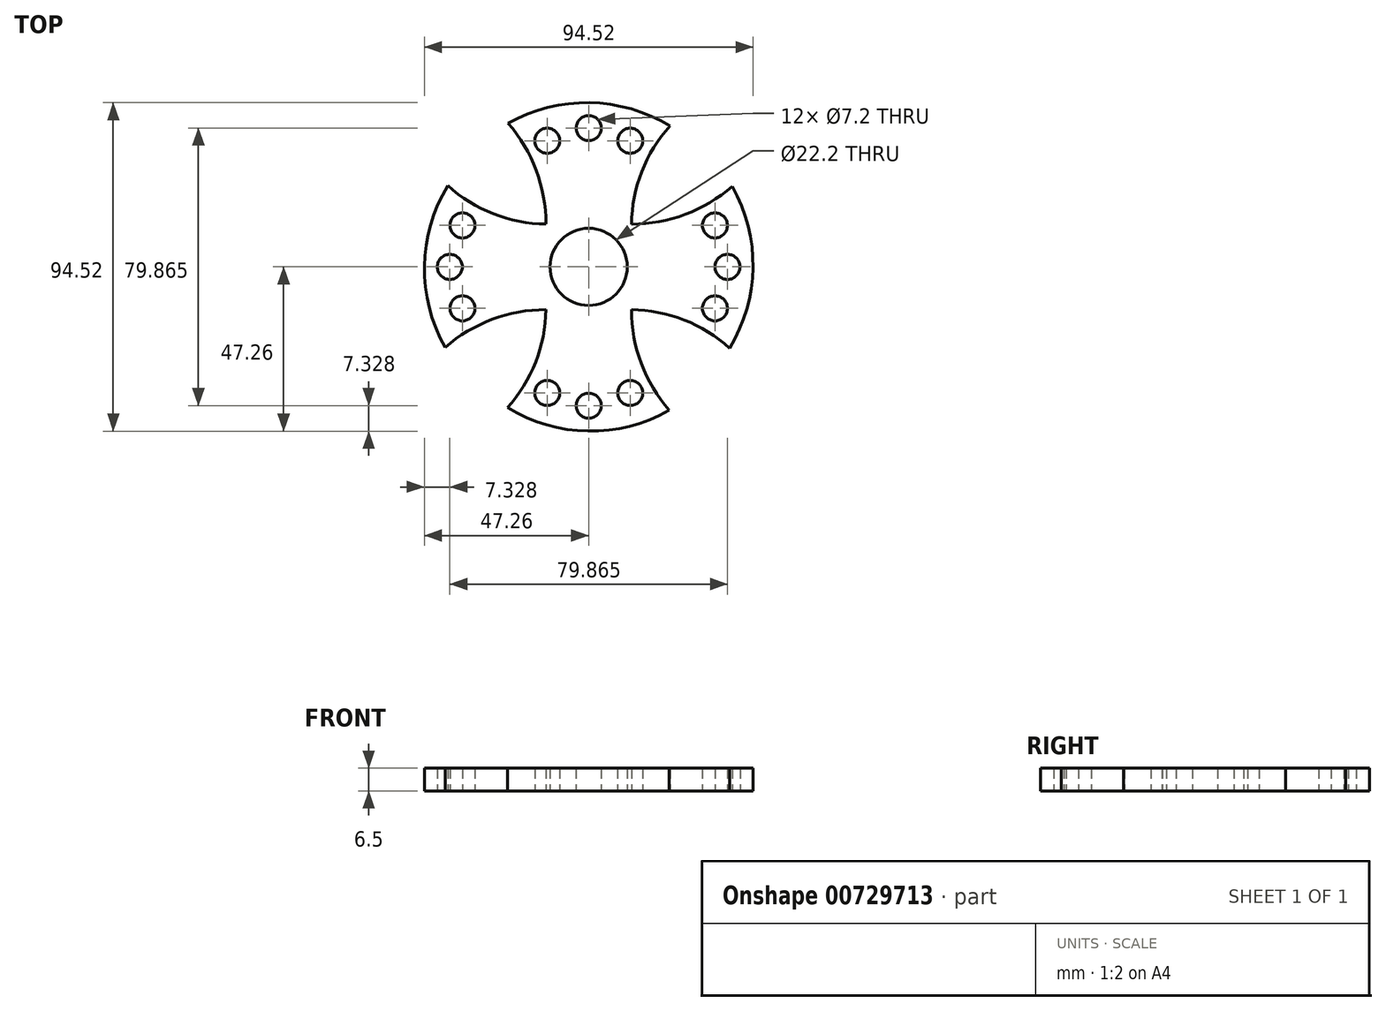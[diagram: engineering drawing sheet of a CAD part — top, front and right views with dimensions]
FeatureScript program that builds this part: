
annotation { "Feature Type Name" : "Feature", "Feature Type Description" : "" }
export const myFeature = defineFeature(function(context is Context, id is Id, definition is map)
    precondition{}
    {
        {
            var Q0;
            Q0=qCreatedBy(makeId("Top.planeOp"),FACE);
            var sketch = newSketch(context, id + "F0", { "sketchPlane" : qUnion([Q0])});
            skCircle(sketch, "E0", {"center": v(0, 0) * mm, "radius": 11.1 * mm});
            skCircle(sketch, "E1", {"center": v(0, 0) * mm, "radius": 14 * mm});
            skCircle(sketch, "E2", {"center": v(0, 39.93) * mm, "radius": 3.6 * mm});
            skCircle(sketch, "E3", {"center": v(-11.93, 36.3) * mm, "radius": 3.6 * mm});
            skArc(sketch, "E4", {"start": v(-14, 0) * mm, "mid": v(-13.33, 21.8) * mm, "end": v(-23.15, 41.28) * mm});
            skArc(sketch, "E5", {"start": v(23.39, 40.5) * mm, "mid": v(13.42, 21.48) * mm, "end": v(14, 0) * mm});
            skArc(sketch, "E6", {"start": v(23.39, 40.5) * mm, "mid": v(0.22, 47.25) * mm, "end": v(-23.15, 41.28) * mm});
            skCircle(sketch, "E7.MirrorC", {"center": v(11.93, 36.3) * mm, "radius": 3.6 * mm});
            skArc(sketch, "E8.1.0", {"start": v(-40.5, 23.39) * mm, "mid": v(-47.25, 0.22) * mm, "end": v(-41.28, -23.15) * mm});
            skCircle(sketch, "E8.1.1", {"center": v(-39.93, 0) * mm, "radius": 3.6 * mm});
            skCircle(sketch, "E8.1.2", {"center": v(-36.3, 11.93) * mm, "radius": 3.6 * mm});
            skCircle(sketch, "E8.1.3", {"center": v(-36.3, -11.93) * mm, "radius": 3.6 * mm});
            skArc(sketch, "E8.1.4", {"start": v(0, -14) * mm, "mid": v(-21.8, -13.33) * mm, "end": v(-41.28, -23.15) * mm});
            skArc(sketch, "E8.1.5", {"start": v(-40.5, 23.39) * mm, "mid": v(-21.48, 13.42) * mm, "end": v(0, 14) * mm});
            skArc(sketch, "E8.2.0", {"start": v(-23.39, -40.5) * mm, "mid": v(-0.22, -47.25) * mm, "end": v(23.15, -41.28) * mm});
            skCircle(sketch, "E8.2.1", {"center": v(0, -39.93) * mm, "radius": 3.6 * mm});
            skCircle(sketch, "E8.2.2", {"center": v(-11.93, -36.3) * mm, "radius": 3.6 * mm});
            skCircle(sketch, "E8.2.3", {"center": v(11.93, -36.3) * mm, "radius": 3.6 * mm});
            skArc(sketch, "E8.2.4", {"start": v(14, 0) * mm, "mid": v(13.33, -21.8) * mm, "end": v(23.15, -41.28) * mm});
            skArc(sketch, "E8.2.5", {"start": v(-23.39, -40.5) * mm, "mid": v(-13.42, -21.48) * mm, "end": v(-14, 0) * mm});
            skArc(sketch, "E8.3.0", {"start": v(40.5, -23.39) * mm, "mid": v(47.25, -0.22) * mm, "end": v(41.28, 23.15) * mm});
            skCircle(sketch, "E8.3.1", {"center": v(39.93, 0) * mm, "radius": 3.6 * mm});
            skCircle(sketch, "E8.3.2", {"center": v(36.3, -11.93) * mm, "radius": 3.6 * mm});
            skCircle(sketch, "E8.3.3", {"center": v(36.3, 11.93) * mm, "radius": 3.6 * mm});
            skArc(sketch, "E8.3.4", {"start": v(0, 14) * mm, "mid": v(21.8, 13.33) * mm, "end": v(41.28, 23.15) * mm});
            skArc(sketch, "E8.3.5", {"start": v(40.5, -23.39) * mm, "mid": v(21.48, -13.42) * mm, "end": v(0, -14) * mm});
            skSolve(sketch);
        }
        {
            var Q0;
            {var subQ0=sQuery(id+"F0.wireOp",EDGE,"E8.1.5");var subQ1=sQuery(id+"F0.wireOp",EDGE,"E1");var subQ3=makeQuery(id+"F0.imprint","INTERSECT",VERTEX,{"derivedFrom":[subQ1,subQ0]});Q0=makeQuery(id+"F0.imprint","IMPRINT",FACE,{"disambiguationData":[TD([[makeQuery(id+"F0.imprint","IMPRINT",EDGE,{"disambiguationData":[TD([[subQ3,1.0]])],"derivedFrom":subQ1}),1.0]])]});}
            var Q1;
            {var subQ0=sQuery(id+"F0.wireOp",EDGE,"E8.3.4");var subQ1=sQuery(id+"F0.wireOp",EDGE,"E1");var subQ3=makeQuery(id+"F0.imprint","INTERSECT",VERTEX,{"derivedFrom":[subQ1,subQ0]});Q1=makeQuery(id+"F0.imprint","IMPRINT",FACE,{"disambiguationData":[TD([[makeQuery(id+"F0.imprint","IMPRINT",EDGE,{"disambiguationData":[TD([[subQ3,-1.0]])],"derivedFrom":subQ1}),1.0]])]});}
            var Q2;
            {var subQ6=sQuery(id+"F0.wireOp",EDGE,"E8.3.0");Q2=makeQuery(id+"F0.imprint","IMPRINT",FACE,{"disambiguationData":[TD([[makeQuery(id+"F0.imprint","IMPRINT",EDGE,{"derivedFrom":subQ6}),1.0]])]});}
            var Q3;
            {var subQ0=sQuery(id+"F0.wireOp",EDGE,"E8.2.4");var subQ1=sQuery(id+"F0.wireOp",EDGE,"E1");var subQ3=makeQuery(id+"F0.imprint","INTERSECT",VERTEX,{"derivedFrom":[subQ1,subQ0]});Q3=makeQuery(id+"F0.imprint","IMPRINT",FACE,{"disambiguationData":[TD([[makeQuery(id+"F0.imprint","IMPRINT",EDGE,{"disambiguationData":[TD([[subQ3,-1.0]])],"derivedFrom":subQ1}),1.0]])]});}
            var Q4;
            {var subQ0=sQuery(id+"F0.wireOp",EDGE,"E5");var subQ1=sQuery(id+"F0.wireOp",EDGE,"E1");var subQ3=makeQuery(id+"F0.imprint","INTERSECT",VERTEX,{"derivedFrom":[subQ1,subQ0]});Q4=makeQuery(id+"F0.imprint","IMPRINT",FACE,{"disambiguationData":[TD([[makeQuery(id+"F0.imprint","IMPRINT",EDGE,{"disambiguationData":[TD([[subQ3,1.0]])],"derivedFrom":subQ1}),1.0]])]});}
            var Q5;
            {var subQ0=sQuery(id+"F0.wireOp",EDGE,"E5");var subQ1=sQuery(id+"F0.wireOp",EDGE,"E1");var subQ2=makeQuery(id+"F0.imprint","INTERSECT",VERTEX,{"derivedFrom":[subQ1,subQ0]});Q5=makeQuery(id+"F0.imprint","IMPRINT",FACE,{"disambiguationData":[TD([[makeQuery(id+"F0.imprint","IMPRINT",EDGE,{"disambiguationData":[TD([[subQ2,-1.0]])],"derivedFrom":subQ1}),-1.0]])]});}
            var Q6;
            {var subQ0=sQuery(id+"F0.wireOp",EDGE,"E8.1.4");var subQ1=sQuery(id+"F0.wireOp",EDGE,"E1");var subQ3=makeQuery(id+"F0.imprint","INTERSECT",VERTEX,{"derivedFrom":[subQ1,subQ0]});Q6=makeQuery(id+"F0.imprint","IMPRINT",FACE,{"disambiguationData":[TD([[makeQuery(id+"F0.imprint","IMPRINT",EDGE,{"disambiguationData":[TD([[subQ3,-1.0]])],"derivedFrom":subQ1}),1.0]])]});}
            var Q7;
            {var subQ0=sQuery(id+"F0.wireOp",EDGE,"E8.2.5");var subQ1=sQuery(id+"F0.wireOp",EDGE,"E1");var subQ3=makeQuery(id+"F0.imprint","INTERSECT",VERTEX,{"derivedFrom":[subQ1,subQ0]});Q7=makeQuery(id+"F0.imprint","IMPRINT",FACE,{"disambiguationData":[TD([[makeQuery(id+"F0.imprint","IMPRINT",EDGE,{"disambiguationData":[TD([[subQ3,1.0]])],"derivedFrom":subQ1}),1.0]])]});}
            var Q8;
            {var subQ0=sQuery(id+"F0.wireOp",EDGE,"E8.1.0");Q8=makeQuery(id+"F0.imprint","IMPRINT",FACE,{"disambiguationData":[TD([[makeQuery(id+"F0.imprint","IMPRINT",EDGE,{"derivedFrom":subQ0}),1.0]])]});}
            var Q9;
            {var subQ0=sQuery(id+"F0.wireOp",EDGE,"E8.2.0");Q9=makeQuery(id+"F0.imprint","IMPRINT",FACE,{"disambiguationData":[TD([[makeQuery(id+"F0.imprint","IMPRINT",EDGE,{"derivedFrom":subQ0}),1.0]])]});}
            var Q10;
            Q10=makeQuery(id+"F0.imprint","IMPRINT",FACE,{"disambiguationData":[TD([[makeQuery(id+"F0.imprint","IMPRINT",EDGE,{"derivedFrom":sQuery(id+"F0.wireOp",EDGE,"E0")}),-1.0]])]});
            var Q11;
            {var subQ0=sQuery(id+"F0.wireOp",EDGE,"E8.3.5");var subQ1=sQuery(id+"F0.wireOp",EDGE,"E1");var subQ2=makeQuery(id+"F0.imprint","INTERSECT",VERTEX,{"derivedFrom":[subQ1,subQ0]});Q11=makeQuery(id+"F0.imprint","IMPRINT",FACE,{"disambiguationData":[TD([[makeQuery(id+"F0.imprint","IMPRINT",EDGE,{"disambiguationData":[TD([[subQ2,-1.0]])],"derivedFrom":subQ1}),-1.0]])]});}
            var Q12;
            {var subQ0=sQuery(id+"F0.wireOp",EDGE,"E8.3.5");var subQ1=sQuery(id+"F0.wireOp",EDGE,"E1");var subQ3=makeQuery(id+"F0.imprint","INTERSECT",VERTEX,{"derivedFrom":[subQ1,subQ0]});Q12=makeQuery(id+"F0.imprint","IMPRINT",FACE,{"disambiguationData":[TD([[makeQuery(id+"F0.imprint","IMPRINT",EDGE,{"disambiguationData":[TD([[subQ3,1.0]])],"derivedFrom":subQ1}),1.0]])]});}
            var Q13;
            {var subQ0=sQuery(id+"F0.wireOp",EDGE,"E8.2.5");var subQ1=sQuery(id+"F0.wireOp",EDGE,"E1");var subQ2=makeQuery(id+"F0.imprint","INTERSECT",VERTEX,{"derivedFrom":[subQ1,subQ0]});Q13=makeQuery(id+"F0.imprint","IMPRINT",FACE,{"disambiguationData":[TD([[makeQuery(id+"F0.imprint","IMPRINT",EDGE,{"disambiguationData":[TD([[subQ2,-1.0]])],"derivedFrom":subQ1}),-1.0]])]});}
            var Q14;
            {var subQ0=sQuery(id+"F0.wireOp",EDGE,"E8.1.5");var subQ1=sQuery(id+"F0.wireOp",EDGE,"E1");var subQ2=makeQuery(id+"F0.imprint","INTERSECT",VERTEX,{"derivedFrom":[subQ1,subQ0]});Q14=makeQuery(id+"F0.imprint","IMPRINT",FACE,{"disambiguationData":[TD([[makeQuery(id+"F0.imprint","IMPRINT",EDGE,{"disambiguationData":[TD([[subQ2,-1.0]])],"derivedFrom":subQ1}),-1.0]])]});}
            var Q15;
            {var subQ0=sQuery(id+"F0.wireOp",EDGE,"E4");var subQ1=sQuery(id+"F0.wireOp",EDGE,"E1");var subQ3=makeQuery(id+"F0.imprint","INTERSECT",VERTEX,{"derivedFrom":[subQ1,subQ0]});Q15=makeQuery(id+"F0.imprint","IMPRINT",FACE,{"disambiguationData":[TD([[makeQuery(id+"F0.imprint","IMPRINT",EDGE,{"disambiguationData":[TD([[subQ3,-1.0]])],"derivedFrom":subQ1}),1.0]])]});}
            var Q16;
            Q16=makeQuery(id+"F0.imprint","IMPRINT",FACE,{"disambiguationData":[TD([[makeQuery(id+"F0.imprint","IMPRINT",EDGE,{"derivedFrom":sQuery(id+"F0.wireOp",EDGE,"E2")}),-1.0]])]});
            extrude(context, id + "F1", {"entities" : qUnion([Q0, Q1, Q2, Q3, Q4, Q5, Q6, Q7, Q8, Q9, Q10, Q11, Q12, Q13, Q14, Q15, Q16]), "depth" : 6.5 * mm, "offsetDistance" : 25 * mm});
        }
    });
